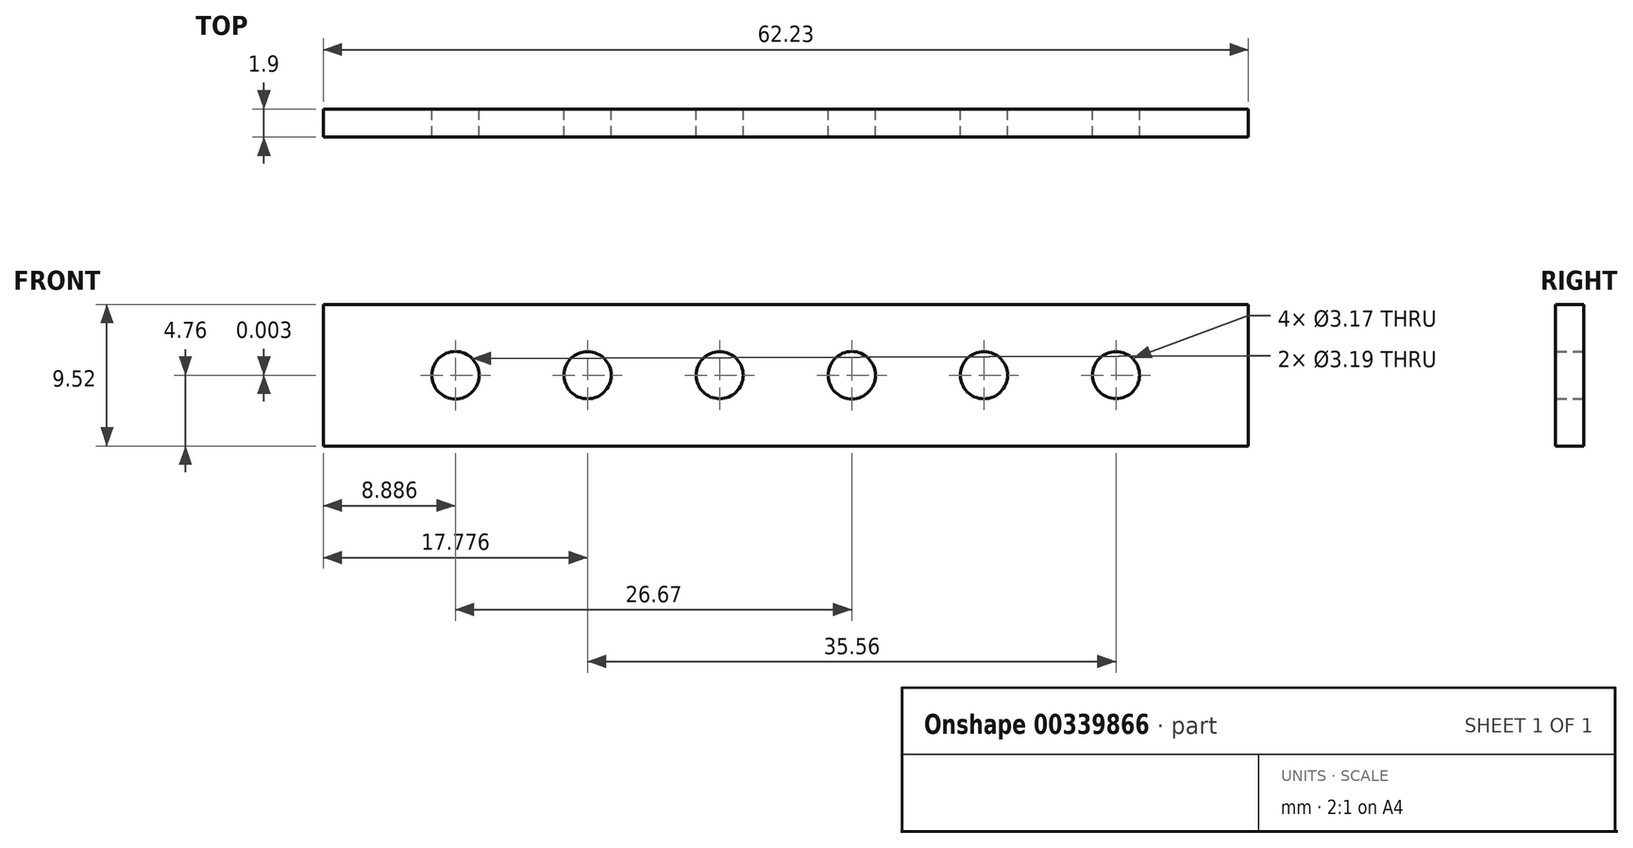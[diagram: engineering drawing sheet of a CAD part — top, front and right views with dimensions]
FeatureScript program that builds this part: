
annotation { "Feature Type Name" : "Feature", "Feature Type Description" : "" }
export const myFeature = defineFeature(function(context is Context, id is Id, definition is map)
    precondition{}
    {
        {
            var Q0;
            Q0=qCreatedBy(makeId("Front.planeOp"),FACE);
            var sketch = newSketch(context, id + "F0", { "sketchPlane" : qUnion([Q0])});
            skLineSegment(sketch, "E0.left", {"start": v(-40.96, 20.31) * mm, "end": v(-40.96, 10.79) * mm});
            skCircle(sketch, "E1", {"center": v(-32.07, 15.55) * mm, "radius": 1.6 * mm});
            skCircle(sketch, "E2", {"center": v(-23.18, 15.55) * mm, "radius": 1.59 * mm});
            skCircle(sketch, "E3", {"center": v(-14.3, 15.55) * mm, "radius": 1.58 * mm});
            skCircle(sketch, "E4", {"center": v(-5.4, 15.55) * mm, "radius": 1.6 * mm});
            skCircle(sketch, "E5", {"center": v(3.49, 15.55) * mm, "radius": 1.59 * mm});
            skCircle(sketch, "E6", {"center": v(12.38, 15.55) * mm, "radius": 1.58 * mm});
            skLineSegment(sketch, "E7", {"start": v(-40.96, 20.31) * mm, "end": v(21.27, 20.31) * mm});
            skLineSegment(sketch, "E8", {"start": v(-40.96, 10.79) * mm, "end": v(21.27, 10.79) * mm});
            skLineSegment(sketch, "E9", {"start": v(21.27, 10.79) * mm, "end": v(21.27, 20.31) * mm});
            skSolve(sketch);
        }
        {
            var Q0;
            Q0=makeQuery(id+"F0.imprint","IMPRINT",FACE,{"disambiguationData":[TD([[makeQuery(id+"F0.imprint","IMPRINT",EDGE,{"derivedFrom":sQuery(id+"F0.wireOp",EDGE,"E0.left")}),1.0]])]});
            extrude(context, id + "F1", {"entities" : qUnion([Q0]), "depth" : 1.9 * mm});
        }
    });
